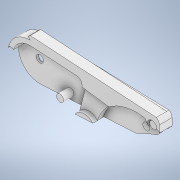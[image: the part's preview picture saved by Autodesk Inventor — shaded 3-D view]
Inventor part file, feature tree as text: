
AUTODESK INVENTOR PART (.ipt)
format: ipt  version: 2022 (Build 260153000, 153)  size: 244,736 bytes
history: native  units: in
note: dims shown in document units (in); Inventor stores cm internally (conversion verified against a paired STEP export)
features: extrude x6, sketch x6, other x1
ambient origin geometry x8: Origin, YZ Plane, XZ Plane, XY Plane, X Axis, Y Axis, Z Axis, Center Point
bodies: Body1 (feature_tree)
feature tree (13):
  other  "Sólido1"
  extrude  "Extrusión1"  Depth=0.0984in
  extrude  "Extrusión2"  Depth=0.5906in
  extrude  "Extrusión3"  Depth=0.0984in
  extrude  "Extrusión6"  Depth=0.1181in
  extrude  "Extrusión7"  Depth=0.1575in
  extrude  "Extrusión8"  Depth=0.0787in
  sketch  "Boceto1"  dims[d9=0.0984in d10=0.0984in]
  sketch  "Boceto2"  dims[d11=1.5354in d12=0.5906in]
  sketch  "Boceto3"  dims[d13=0.2362in d14=0.0984in]
  sketch  "Boceto7"  dims[d15=0.1378in d16=0.1181in]
  sketch  "Boceto8"  dims[d17=0.1575in d18=0.0984in]
  sketch  "Boceto9"  dims[d19=0.128in d20=0.0787in d21=0.0787in d22=0.2205in d23=0.2244in d25=0.0315in d26=0.0in d27=0.0787in d28=0.0in d31=0.1575in d32=0.0in d35=0.0984in d36=0.0787in d39=0.0984in d40=0.0984in d41=0.0394in d42=0.0in d43=0.0157in d44=0.0in d45=0.0984in d46=0.0787in d47=0.063in d48=0.0in d33=0.0197in d34=0.0344in]
